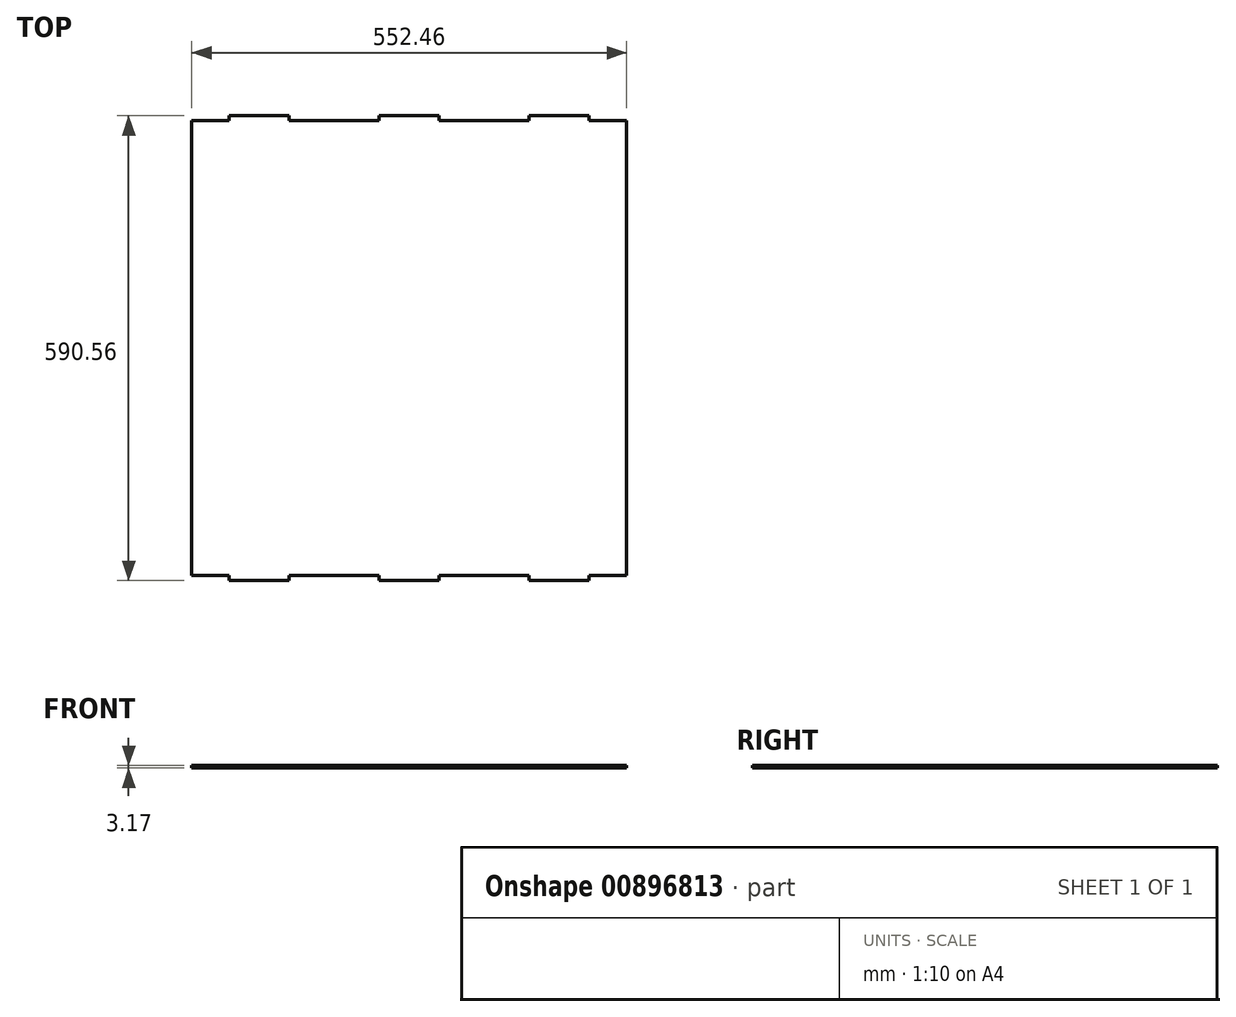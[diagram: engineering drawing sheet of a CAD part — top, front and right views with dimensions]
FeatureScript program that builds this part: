
annotation { "Feature Type Name" : "Feature", "Feature Type Description" : "" }
export const myFeature = defineFeature(function(context is Context, id is Id, definition is map)
    precondition{}
    {
        {
            var Q0;
            Q0=qCreatedBy(makeId("Top.planeOp"),FACE);
            var sketch = newSketch(context, id + "F0", { "sketchPlane" : qUnion([Q0])});
            skLineSegment(sketch, "E0.bottom", {"start": v(276.23, -288.93) * mm, "end": v(228.6, -288.93) * mm});
            skLineSegment(sketch, "E0.top", {"start": v(276.22, 288.93) * mm, "end": v(228.6, 288.93) * mm});
            skLineSegment(sketch, "E0.left", {"start": v(276.23, -288.93) * mm, "end": v(276.23, 288.93) * mm});
            skLineSegment(sketch, "E0.right", {"start": v(-276.23, -288.93) * mm, "end": v(-276.23, 288.93) * mm});
            skPoint(sketch, "E0.middle", {"position": v(0, 0) * mm});
            skLineSegment(sketch, "E1", {"start": v(0, 0) * mm, "end": v(0, 423.4) * mm, "construction": true});
            skLineSegment(sketch, "E2", {"start": v(0, 423.4) * mm, "end": v(0, -399.83) * mm, "construction": true});
            skLineSegment(sketch, "E3.top", {"start": v(-38.1, 295.28) * mm, "end": v(38.1, 295.28) * mm});
            skLineSegment(sketch, "E3.left", {"start": v(-38.1, 288.93) * mm, "end": v(-38.1, 295.28) * mm});
            skLineSegment(sketch, "E3.right", {"start": v(38.1, 288.93) * mm, "end": v(38.1, 295.28) * mm});
            skLineSegment(sketch, "E4.trimOffspring", {"start": v(-38.1, 288.93) * mm, "end": v(-152.4, 288.93) * mm});
            skLineSegment(sketch, "E5.top", {"start": v(-228.6, 295.28) * mm, "end": v(-152.4, 295.28) * mm});
            skLineSegment(sketch, "E5.left", {"start": v(-228.6, 288.93) * mm, "end": v(-228.6, 295.28) * mm});
            skLineSegment(sketch, "E5.right", {"start": v(-152.4, 288.93) * mm, "end": v(-152.4, 295.28) * mm});
            skLineSegment(sketch, "E6.trimOffspring", {"start": v(-228.6, 288.93) * mm, "end": v(-276.23, 288.93) * mm});
            skLineSegment(sketch, "E7.bottom", {"start": v(152.4, 295.28) * mm, "end": v(228.6, 295.28) * mm});
            skLineSegment(sketch, "E7.left", {"start": v(152.4, 295.28) * mm, "end": v(152.4, 288.93) * mm});
            skLineSegment(sketch, "E7.right", {"start": v(228.6, 295.28) * mm, "end": v(228.6, 288.93) * mm});
            skLineSegment(sketch, "E8.trimOffspring", {"start": v(152.4, 288.93) * mm, "end": v(38.1, 288.93) * mm});
            skLineSegment(sketch, "E9.top", {"start": v(-38.1, -295.28) * mm, "end": v(38.1, -295.28) * mm});
            skLineSegment(sketch, "E9.left", {"start": v(-38.1, -288.93) * mm, "end": v(-38.1, -295.28) * mm});
            skLineSegment(sketch, "E9.right", {"start": v(38.1, -288.93) * mm, "end": v(38.1, -295.28) * mm});
            skLineSegment(sketch, "E10.top", {"start": v(-152.4, -295.28) * mm, "end": v(-228.6, -295.28) * mm});
            skLineSegment(sketch, "E10.left", {"start": v(-152.4, -288.93) * mm, "end": v(-152.4, -295.28) * mm});
            skLineSegment(sketch, "E10.right", {"start": v(-228.6, -288.93) * mm, "end": v(-228.6, -295.28) * mm});
            skLineSegment(sketch, "E11.top", {"start": v(152.4, -295.28) * mm, "end": v(228.6, -295.28) * mm});
            skLineSegment(sketch, "E11.left", {"start": v(152.4, -288.93) * mm, "end": v(152.4, -295.28) * mm});
            skLineSegment(sketch, "E11.right", {"start": v(228.6, -288.93) * mm, "end": v(228.6, -295.28) * mm});
            skLineSegment(sketch, "E12.trimOffspring", {"start": v(-38.1, -288.93) * mm, "end": v(-152.4, -288.93) * mm});
            skLineSegment(sketch, "E13.trimOffspring", {"start": v(152.4, -288.93) * mm, "end": v(38.1, -288.93) * mm});
            skLineSegment(sketch, "E14.trimOffspring", {"start": v(-228.6, -288.93) * mm, "end": v(-276.23, -288.93) * mm});
            skSolve(sketch);
        }
        {
            var Q0;
            Q0 = qSketchRegion(id + "F0", true);
            extrude(context, id + "F1", {"entities" : qUnion([Q0]), "depth" : 3.17 * mm, "offsetDistance" : 25.4 * mm});
        }
    });
